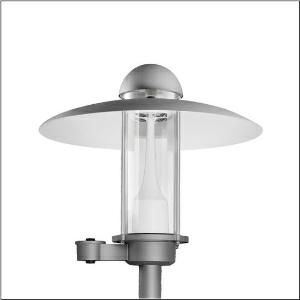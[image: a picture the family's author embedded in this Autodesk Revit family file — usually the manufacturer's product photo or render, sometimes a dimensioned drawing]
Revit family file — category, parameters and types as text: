
# Revit family: city-light_elegance___st1_2a_5xa5263et14h000032_f584
name_source: partatom
category: Lighting Fixtures
units: mm (PartAtom-declared; Revit-internal decimal feet)

## family parameters
Cut with Voids When Loaded = No
Host = Face
Light Source = No
Part Type = Normal
Room Calculation Point = No
Round Connector Dimension = Use Diameter
Shared = No

## types (1)
- --- (1 x LED, 1470 lm, 14.2 W, 3000K)
    Apparent Load = 14 VA
    CIE Flux Codes = 22 62 94 98 100
    Color Rendering = 80
    Color Temperature = 3000K
    Default Elevation = 1800 mm
    Description = City-Light Elegance, mast luminaire, Module 540 Plus, primary light control with 3 zone facetted reflector, of plastic, silver coated, highly specular, structured, primary optical cover: cover, of PMMA, transparent, light distribution: ST1.2a, light emission: direct distribution, primary light characteristic: asymmetric, installation type: post-top, LED, High Power LED, rated luminous flux: 1.470lm, luminous efficacy: 104lm/W, light colour: 830, colour temperature: 3000K, control gear: ECG Smart Interface, control: overheat protection, digital communication interface, time-dependent luminous flux control, flexible luminous flux parameterisation, presetting dimming logarithmic, with terminal, 6-pole, max. 2.5mm², mains connection: 230..240V, AC, 50/60Hz, start of lifetime: 14W, end of service life: 15W, reduction: 8W, luminaire housing, upper part, of aluminium, coated, Siteco® metallic grey (DB 702S), diameter: 750mm, height: 675mm, spigot size: d x l = 76 x 70mm (post-top) | with reducer (optional accessory) 60 x 70mm, post-top mast mounting element, of diecast aluminium, coated, Siteco® metallic grey (DB 702S), Module 540 Plus, traffic white (RAL 9016), Smart Interface below and above, protection rating (complete): IP65, insulation class (complete): insulation class II (safety insulation), certification: CE, ENEC, VDE, packaging unit: 1 piece

Light Distribution: ST1.2a
    Height = 675 mm
    Lamp = 1 x LED
    Lamp Light Flux = 1470 lm
    Lamp Power = 14.2 W
    Lamp count = 1
    Length = 750 mm
    Luminous efficacy = 104 lm/W
    Manufacturer = Siteco
    ModVariant = No
    Model = 5XA5263ET14H000032
    Number of Poles = 1
    OnlyDefault = Yes
    Power Factor = 1
    Product Name = City-Light Elegance | ST1.2a
    Product group = mast luminaire | pylon top
    ProductGroupID = 6100
    Protection Class = Protection class II
    Protection Degree = IP 65
    RLX_Detail_Level = 1
    RLX_Emergency_Light_Flux = 0 lm
    RLX_Emergency_Type = 0
    RLX_Emergency_Type_DB = No
    RlxData = <blob elided: 72565 chars, md5=7e047d0f>
    Socket = socket
    Standby Power = 0 W
    System Light Flux = 1470 lm
    System Power = 14 W
    Type Comments = factory setting: luminous flux: 100 % | dim-lin: 254 | 516 mA
    Type Image = l_1005991.jpg
    URL = http://relux.com
    VarID = @adj_151413
    Voltage = 0 V
    Weight = 0.00 kg
    Width = 0 mm  [stored 0 ft]

note: [stored X ft] marks values corroborated as IEEE doubles in the binary element streams (Revit-internal decimal feet)

## geometry (parser evidence)
native form markers: Blend x4, Sweep x12
no freeform markers — native parametric forms only
